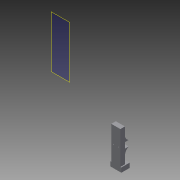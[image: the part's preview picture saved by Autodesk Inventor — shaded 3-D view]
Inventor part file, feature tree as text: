
AUTODESK INVENTOR PART (.ipt)
format: ipt  version: 2015 (Build 190159000, 159)  size: 121,344 bytes
history: native  units: in
note: dims shown in document units (in); Inventor stores cm internally (conversion verified against a paired STEP export)
features: other x3, plane x1
ambient origin geometry x8: Origin, YZ Plane, XZ Plane, XY Plane, X Axis, Y Axis, Z Axis, Center Point
bodies: Solid1 (feature_tree)
feature tree (4):
  other  "side piece.ipt"
  other  "Solid1::side piece.ipt"
  other  "TaggingFeature1"
  plane  "Work Plane1"
